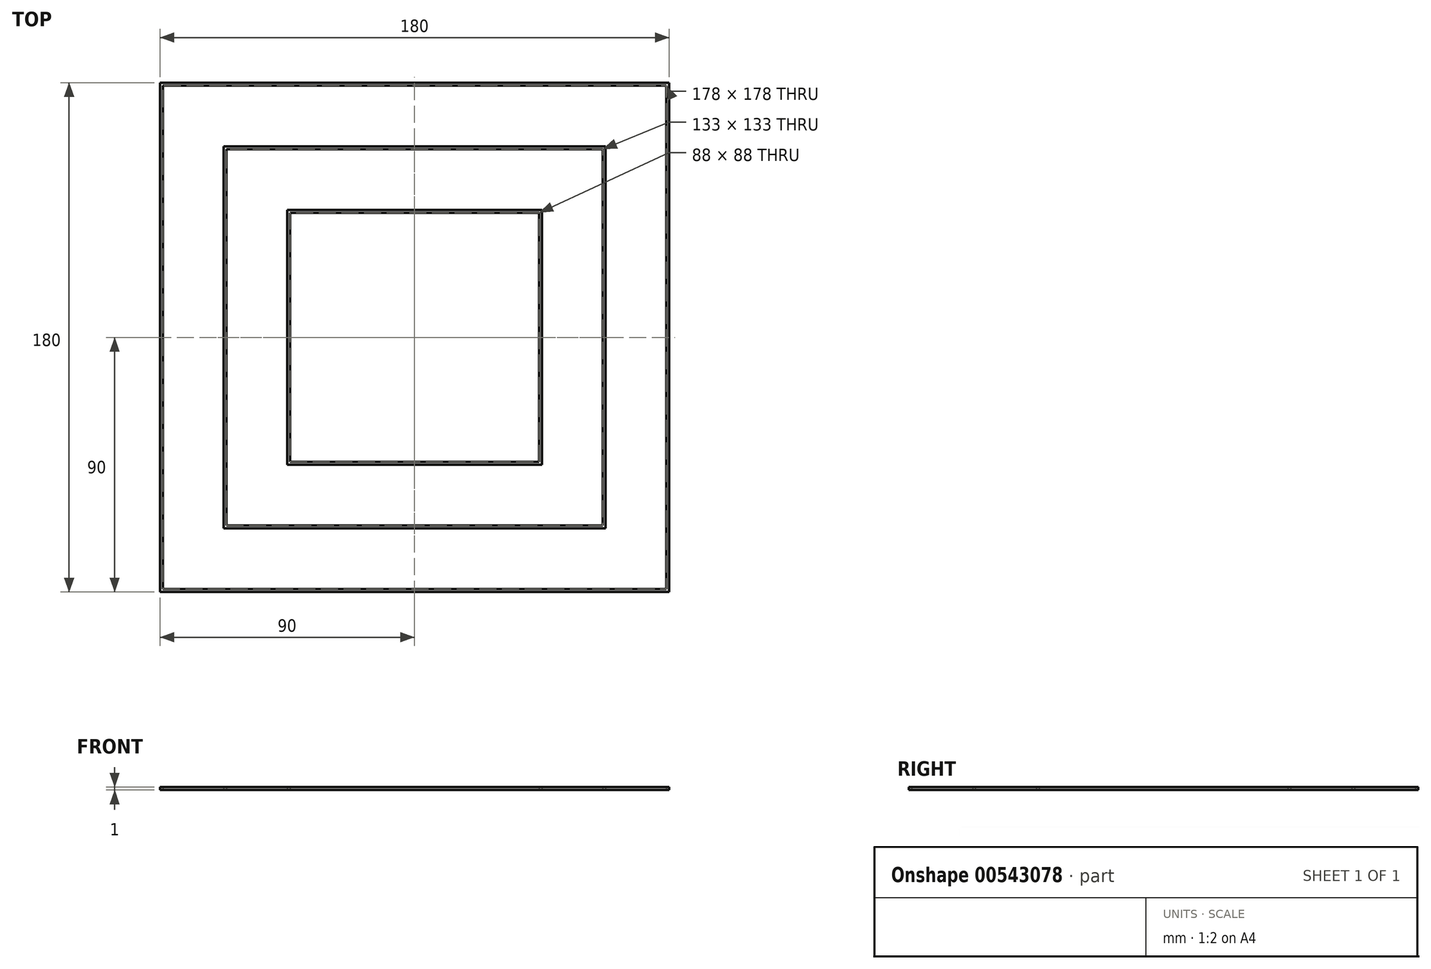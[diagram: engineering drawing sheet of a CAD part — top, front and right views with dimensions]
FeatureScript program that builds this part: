
annotation { "Feature Type Name" : "Feature", "Feature Type Description" : "" }
export const myFeature = defineFeature(function(context is Context, id is Id, definition is map)
    precondition{}
    {
        {
            var Q0;
            Q0=qCreatedBy(makeId("Top.planeOp"),FACE);
            var sketch = newSketch(context, id + "F0", { "sketchPlane" : qUnion([Q0])});
            skLineSegment(sketch, "E0.bottom", {"start": v(90, -90) * mm, "end": v(-90, -90) * mm});
            skLineSegment(sketch, "E0.top", {"start": v(90, 90) * mm, "end": v(-90, 90) * mm});
            skLineSegment(sketch, "E0.left", {"start": v(90, -90) * mm, "end": v(90, 90) * mm});
            skLineSegment(sketch, "E0.right", {"start": v(-90, -90) * mm, "end": v(-90, 90) * mm});
            skPoint(sketch, "E0.middle", {"position": v(0, 0) * mm});
            skLineSegment(sketch, "E1.bottom", {"start": v(67.5, -67.5) * mm, "end": v(-67.5, -67.5) * mm});
            skLineSegment(sketch, "E1.top", {"start": v(67.5, 67.5) * mm, "end": v(-67.5, 67.5) * mm});
            skLineSegment(sketch, "E1.left", {"start": v(67.5, -67.5) * mm, "end": v(67.5, 67.5) * mm});
            skLineSegment(sketch, "E1.right", {"start": v(-67.5, -67.5) * mm, "end": v(-67.5, 67.5) * mm});
            skLineSegment(sketch, "E2.bottom", {"start": v(45, -45) * mm, "end": v(-45, -45) * mm});
            skLineSegment(sketch, "E2.top", {"start": v(45, 45) * mm, "end": v(-45, 45) * mm});
            skLineSegment(sketch, "E2.left", {"start": v(45, -45) * mm, "end": v(45, 45) * mm});
            skLineSegment(sketch, "E2.right", {"start": v(-45, -45) * mm, "end": v(-45, 45) * mm});
            skLineSegment(sketch, "E3.0", {"start": v(-89, -89) * mm, "end": v(-89, 89) * mm});
            skLineSegment(sketch, "E3.1", {"start": v(89, -89) * mm, "end": v(-89, -89) * mm});
            skLineSegment(sketch, "E3.2", {"start": v(89, -89) * mm, "end": v(89, 89) * mm});
            skLineSegment(sketch, "E3.3", {"start": v(89, 89) * mm, "end": v(-89, 89) * mm});
            skLineSegment(sketch, "E4.0", {"start": v(-66.5, -66.5) * mm, "end": v(-66.5, 66.5) * mm});
            skLineSegment(sketch, "E4.1", {"start": v(66.5, -66.5) * mm, "end": v(-66.5, -66.5) * mm});
            skLineSegment(sketch, "E4.2", {"start": v(66.5, -66.5) * mm, "end": v(66.5, 66.5) * mm});
            skLineSegment(sketch, "E4.3", {"start": v(66.5, 66.5) * mm, "end": v(-66.5, 66.5) * mm});
            skLineSegment(sketch, "E5.0", {"start": v(-44, -44) * mm, "end": v(-44, 44) * mm});
            skLineSegment(sketch, "E5.1", {"start": v(44, -44) * mm, "end": v(-44, -44) * mm});
            skLineSegment(sketch, "E5.2", {"start": v(44, -44) * mm, "end": v(44, 44) * mm});
            skLineSegment(sketch, "E5.3", {"start": v(44, 44) * mm, "end": v(-44, 44) * mm});
            skSolve(sketch);
        }
        {
            var Q0;
            Q0=makeQuery(id+"F0.imprint","IMPRINT",FACE,{"disambiguationData":[TD([[makeQuery(id+"F0.imprint","IMPRINT",EDGE,{"derivedFrom":sQuery(id+"F0.wireOp",EDGE,"E0.bottom")}),-1.0]])]});
            var Q1;
            Q1=makeQuery(id+"F0.imprint","IMPRINT",FACE,{"disambiguationData":[TD([[makeQuery(id+"F0.imprint","IMPRINT",EDGE,{"derivedFrom":sQuery(id+"F0.wireOp",EDGE,"E2.bottom")}),-1.0]])]});
            var Q2;
            Q2=makeQuery(id+"F0.imprint","IMPRINT",FACE,{"disambiguationData":[TD([[makeQuery(id+"F0.imprint","IMPRINT",EDGE,{"derivedFrom":sQuery(id+"F0.wireOp",EDGE,"E1.bottom")}),-1.0]])]});
            extrude(context, id + "F1", {"entities" : qUnion([Q0, Q1, Q2]), "depth" : 1 * mm, "offsetDistance" : 25 * mm});
        }
    });
